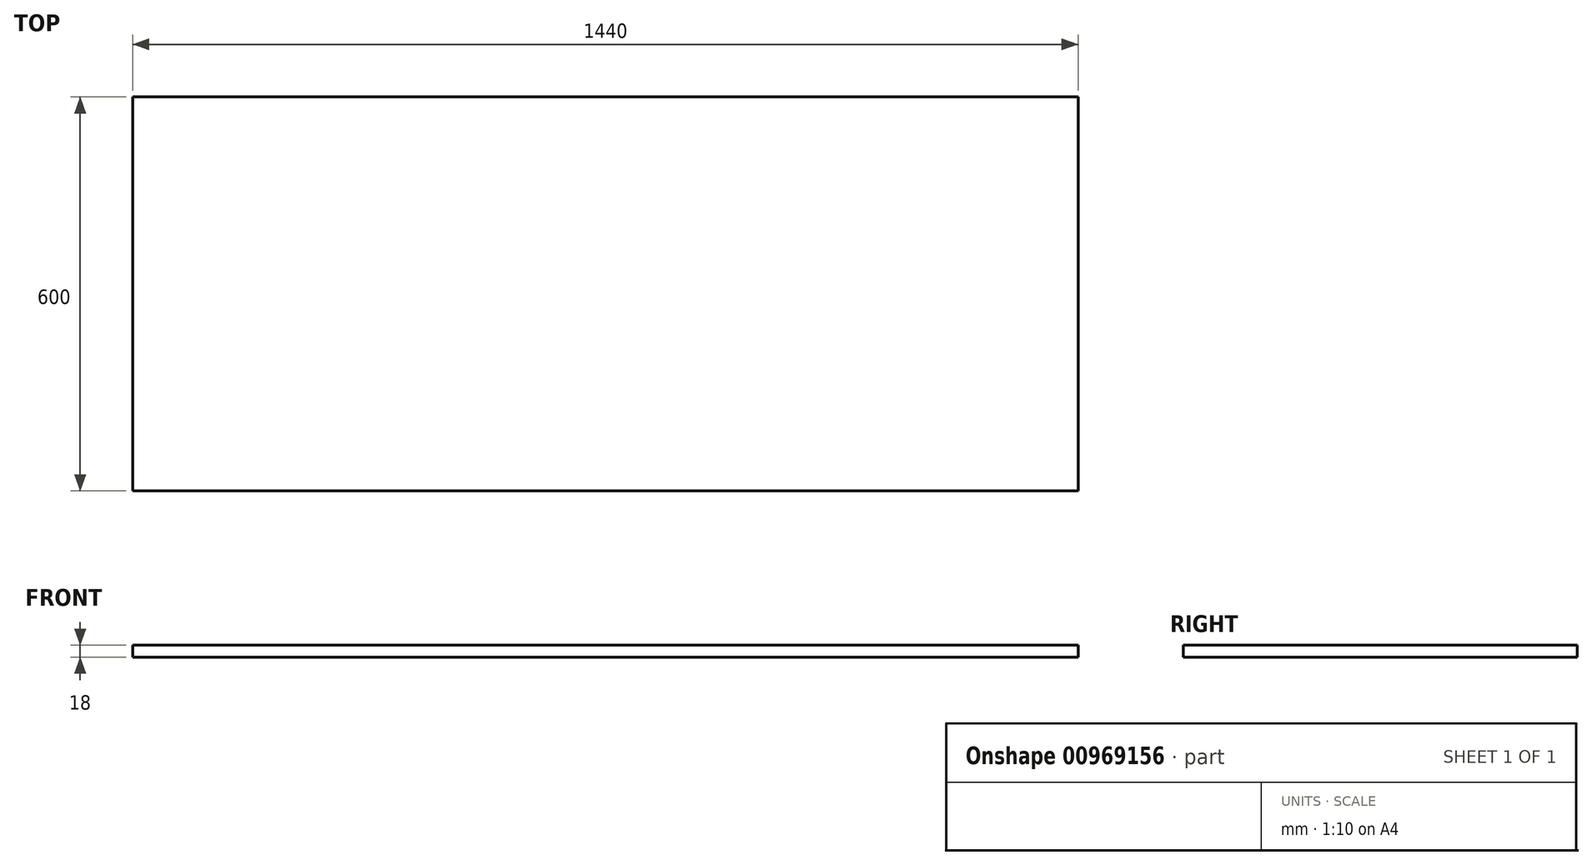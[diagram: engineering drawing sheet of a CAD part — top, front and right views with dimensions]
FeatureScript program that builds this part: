
annotation { "Feature Type Name" : "Feature", "Feature Type Description" : "" }
export const myFeature = defineFeature(function(context is Context, id is Id, definition is map)
    precondition{}
    {
        {
            var Q0;
            Q0=qCreatedBy(makeId("Top.planeOp"),FACE);
            var sketch = newSketch(context, id + "F0", { "sketchPlane" : qUnion([Q0])});
            skLineSegment(sketch, "E0.bottom", {"start": v(0, 0) * mm, "end": v(1440, 0) * mm});
            skLineSegment(sketch, "E0.top", {"start": v(0, 600) * mm, "end": v(1440, 600) * mm});
            skLineSegment(sketch, "E0.left", {"start": v(0, 0) * mm, "end": v(0, 600) * mm});
            skLineSegment(sketch, "E0.right", {"start": v(1440, 0) * mm, "end": v(1440, 600) * mm});
            skSolve(sketch);
        }
        {
            var Q0;
            Q0 = qSketchRegion(id + "F0", true);
            extrude(context, id + "F1", {"entities" : qUnion([Q0]), "depth" : 18 * mm, "offsetDistance" : 25 * mm});
        }
    });
